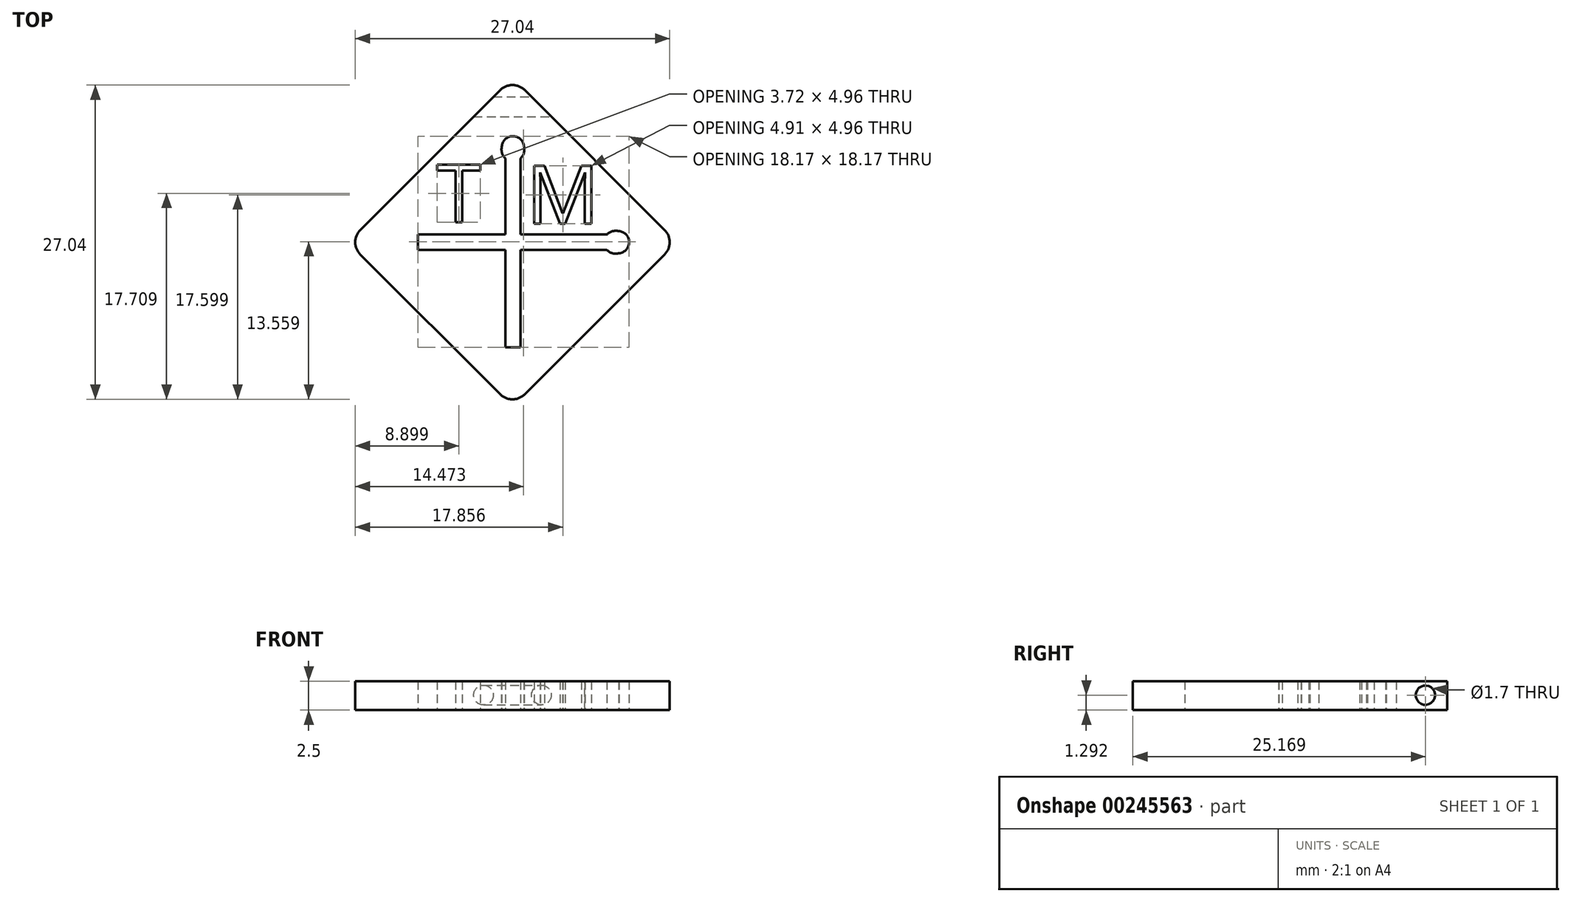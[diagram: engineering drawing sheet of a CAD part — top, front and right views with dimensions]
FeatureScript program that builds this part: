
annotation { "Feature Type Name" : "Feature", "Feature Type Description" : "" }
export const myFeature = defineFeature(function(context is Context, id is Id, definition is map)
    precondition{}
    {
        {
            var Q0;
            Q0=qCreatedBy(makeId("Top.planeOp"),FACE);
            var sketch = newSketch(context, id + "F0", { "sketchPlane" : qUnion([Q0])});
            skLineSegment(sketch, "E0", {"start": v(1.06, -1.06) * mm, "end": v(13.08, -13.08) * mm});
            skLineSegment(sketch, "E1", {"start": v(13.08, -15.2) * mm, "end": v(1.06, -27.22) * mm});
            skLineSegment(sketch, "E2", {"start": v(-1.06, -27.22) * mm, "end": v(-13.08, -15.2) * mm});
            skLineSegment(sketch, "E3", {"start": v(-13.08, -13.08) * mm, "end": v(-1.06, -1.06) * mm});
            skPoint(sketch, "E4.visualSharp", {"position": v(0, 0) * mm});
            skArc(sketch, "E4.filletArc", {"start": v(1.06, -1.06) * mm, "mid": v(0, -0.62) * mm, "end": v(-1.06, -1.06) * mm});
            skPoint(sketch, "E5.visualSharp", {"position": v(-14.14, -14.14) * mm});
            skArc(sketch, "E5.filletArc", {"start": v(-13.08, -13.08) * mm, "mid": v(-13.52, -14.14) * mm, "end": v(-13.08, -15.2) * mm});
            skPoint(sketch, "E6.visualSharp", {"position": v(14.14, -14.14) * mm});
            skArc(sketch, "E6.filletArc", {"start": v(13.08, -15.2) * mm, "mid": v(13.52, -14.14) * mm, "end": v(13.08, -13.08) * mm});
            skPoint(sketch, "E7.visualSharp", {"position": v(0, -28.28) * mm});
            skArc(sketch, "E7.filletArc", {"start": v(-1.06, -27.22) * mm, "mid": v(0, -27.66) * mm, "end": v(1.06, -27.22) * mm});
            skLineSegment(sketch, "E8", {"start": v(0, 0) * mm, "end": v(0, -31.86) * mm, "construction": true});
            skLineSegment(sketch, "E9", {"start": v(-14.14, -14.14) * mm, "end": v(14.14, -14.14) * mm, "construction": true});
            skLineSegment(sketch, "E10", {"start": v(-8.13, -13.48) * mm, "end": v(-8.13, -14.8) * mm});
            skLineSegment(sketch, "E11", {"start": v(-8.13, -14.8) * mm, "end": v(8.13, -14.8) * mm});
            skLineSegment(sketch, "E12", {"start": v(8.13, -13.48) * mm, "end": v(-8.13, -13.48) * mm});
            skLineSegment(sketch, "E13", {"start": v(-8.13, -13.48) * mm, "end": v(0, -13.48) * mm, "construction": true});
            skLineSegment(sketch, "E14", {"start": v(0, -13.48) * mm, "end": v(8.13, -13.48) * mm, "construction": true});
            skArc(sketch, "E15", {"start": v(9.18, -15.1) * mm, "mid": v(10.04, -14.12) * mm, "end": v(9.13, -13.2) * mm});
            skArc(sketch, "E16", {"start": v(9.13, -13.2) * mm, "mid": v(8.6, -13.2) * mm, "end": v(8.13, -13.48) * mm});
            skArc(sketch, "E17", {"start": v(8.13, -14.8) * mm, "mid": v(8.61, -15.1) * mm, "end": v(9.18, -15.1) * mm});
            skLineSegment(sketch, "E18", {"start": v(-0.62, -23.19) * mm, "end": v(0.7, -23.19) * mm});
            skLineSegment(sketch, "E19", {"start": v(0.7, -23.19) * mm, "end": v(0.7, -6.92) * mm});
            skLineSegment(sketch, "E20", {"start": v(-0.62, -6.92) * mm, "end": v(-0.62, -23.19) * mm});
            skLineSegment(sketch, "E21", {"start": v(-0.62, -23.19) * mm, "end": v(-0.62, -15.05) * mm, "construction": true});
            skLineSegment(sketch, "E22", {"start": v(-0.62, -15.05) * mm, "end": v(-0.62, -6.92) * mm, "construction": true});
            skArc(sketch, "E23", {"start": v(0.99, -5.88) * mm, "mid": v(0.02, -5.01) * mm, "end": v(-0.91, -5.92) * mm});
            skArc(sketch, "E24", {"start": v(-0.91, -5.92) * mm, "mid": v(-0.9, -6.46) * mm, "end": v(-0.62, -6.92) * mm});
            skArc(sketch, "E25", {"start": v(0.7, -6.92) * mm, "mid": v(1, -6.44) * mm, "end": v(0.99, -5.88) * mm});
            skText(sketch, "E26", { "text": "T\n", "fontName": "OpenSans-Regular.ttf"});
            skText(sketch, "E27", { "text": "M\n", "fontName": "OpenSans-Regular.ttf"});
            const initialGuessF0  = {"E26": [-0.00654, -0.01243, 1, 0, 0.005], "E27": [0.0012, -0.01254, 1, 0, 0.005]};
            skSetInitialGuess(sketch, initialGuessF0);
            skSolve(sketch);
        }
        {
            var Q0;
            Q0=makeQuery(id+"F0.imprint","IMPRINT",FACE,{"disambiguationData":[TD([[makeQuery(id+"F0.imprint","IMPRINT",EDGE,{"derivedFrom":sQuery(id+"F0.wireOp",EDGE,"E0")}),-1.0]])]});
            extrude(context, id + "F1", {"entities" : qUnion([Q0]), "depth" : 2.5 * mm});
        }
        {
            var Q0;
            Q0=qCreatedBy(makeId("Right.planeOp"),FACE);
            var sketch = newSketch(context, id + "F2", { "sketchPlane" : qUnion([Q0])});
            skCircle(sketch, "E28", {"center": v(-2.5, 1.3) * mm, "radius": 0.85 * mm});
            skSolve(sketch);
        }
        {
            var Q0;
            Q0=qSketchRegion(id+"F2",true);
            extrude(context, id + "F3", {"entities" : qUnion([Q0]), "operationType" : NewBodyOperationType.REMOVE, "endBound" : BoundingType.SYMMETRIC, "oppositeDirection" : true, "depth" : 25 * mm});
        }
    });
